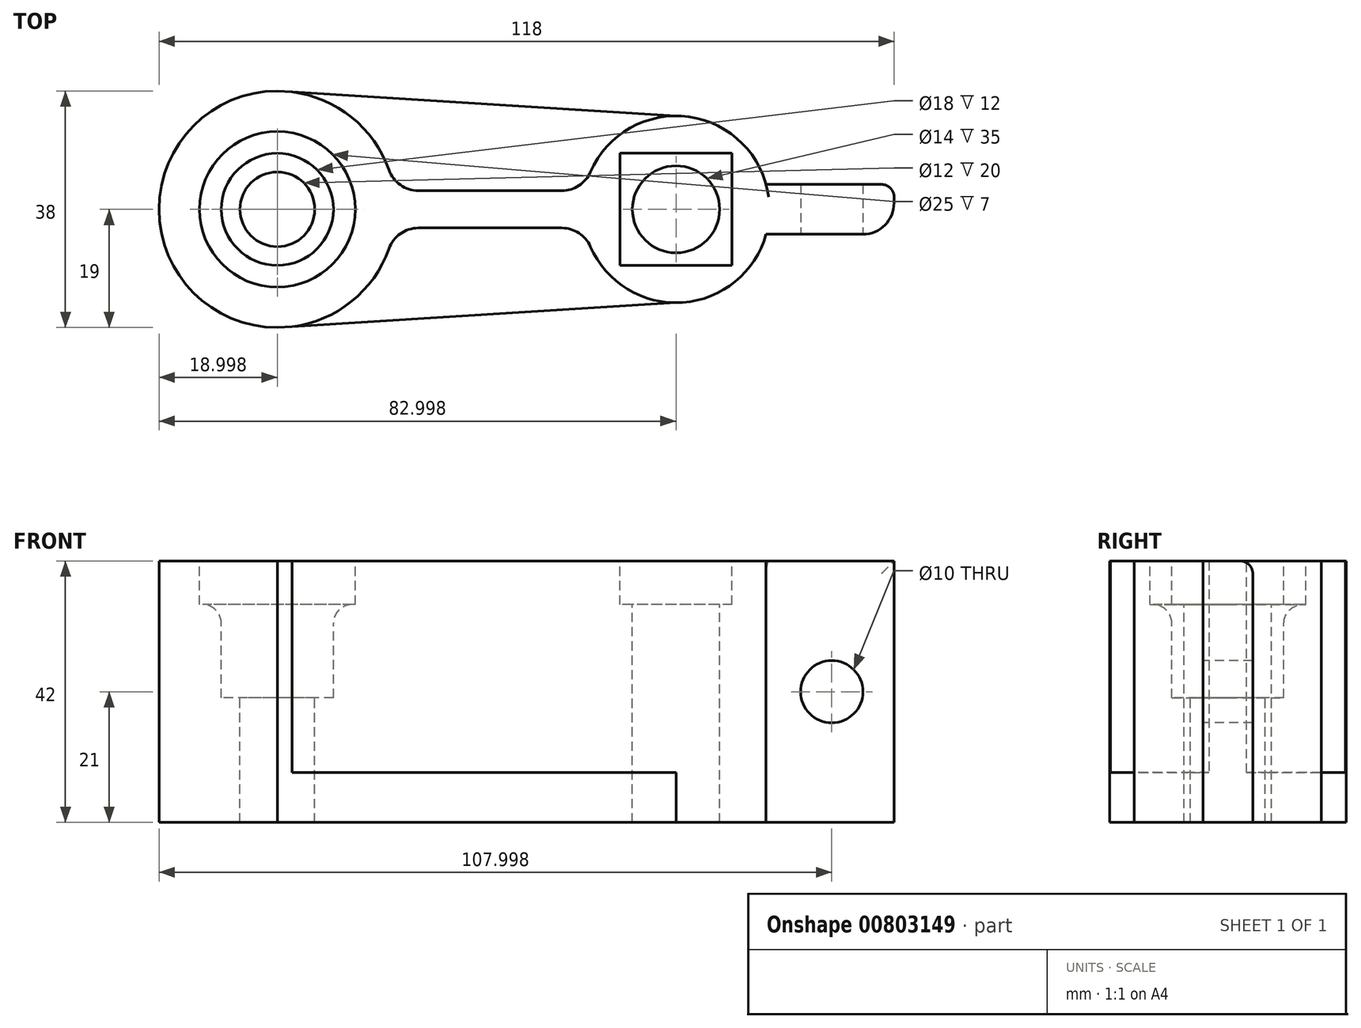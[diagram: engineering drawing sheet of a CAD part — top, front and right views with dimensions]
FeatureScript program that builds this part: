
annotation { "Feature Type Name" : "Feature", "Feature Type Description" : "" }
export const myFeature = defineFeature(function(context is Context, id is Id, definition is map)
    precondition{}
    {
        {
            var Q0;
            Q0=qCreatedBy(makeId("Top.planeOp"),FACE);
            var sketch = newSketch(context, id + "F0", { "sketchPlane" : qUnion([Q0])});
            skArc(sketch, "E0", {"start": v(-57.56, 18.85) * mm, "mid": v(-78.92, 0) * mm, "end": v(-57.56, -18.85) * mm});
            skArc(sketch, "E1", {"start": v(4.08, -15) * mm, "mid": v(19.08, 0) * mm, "end": v(4.08, 15) * mm});
            skLineSegment(sketch, "E2", {"start": v(-59.92, 19) * mm, "end": v(4.08, 15) * mm});
            skLineSegment(sketch, "E3", {"start": v(-59.92, -19) * mm, "end": v(4.08, -15) * mm});
            skLineSegment(sketch, "E4.bottom", {"start": v(39.08, 4) * mm, "end": v(18.53, 4) * mm});
            skLineSegment(sketch, "E4.top", {"start": v(39.08, -4) * mm, "end": v(18.53, -4) * mm});
            skLineSegment(sketch, "E4.left", {"start": v(39.08, 4) * mm, "end": v(39.08, -4) * mm});
            skPoint(sketch, "E4.middle", {"position": v(22.27, 0) * mm});
            skPoint(sketch, "E4.right.start.orphan", {"position": v(5.46, 4) * mm});
            skPoint(sketch, "E5.orphan", {"position": v(5.46, -4) * mm});
            skSolve(sketch);
        }
        {
            var Q0;
            {var subQ0=sQuery(id+"F0.wireOp",EDGE,"E2");var subQ7=sQuery(id+"F0.wireOp",EDGE,"E0");var subQ8=makeQuery(id+"F0.imprint","INTERSECT",VERTEX,{"disambiguationData":[OD(1.0)],"derivedFrom":[subQ7,subQ0]});Q0=makeQuery(id+"F0.imprint","IMPRINT",FACE,{"disambiguationData":[TD([[makeQuery(id+"F0.imprint","IMPRINT",EDGE,{"disambiguationData":[TD([[subQ8,-1.0]])],"derivedFrom":subQ7}),1.0]])]});}
            var Q1;
            {var subQ0=sQuery(id+"F0.wireOp",EDGE,"E4.bottom");Q1=makeQuery(id+"F0.imprint","IMPRINT",FACE,{"disambiguationData":[TD([[makeQuery(id+"F0.imprint","IMPRINT",EDGE,{"derivedFrom":subQ0}),1.0]])]});}
            extrude(context, id + "F1", {"entities" : qUnion([Q0, Q1]), "depth" : 21 * mm, "offsetDistance" : 25 * mm, "hasSecondDirection" : true, "secondDirectionOppositeDirection" : true, "secondDirectionDepth" : 21 * mm});
        }
        {
            var Q0;
            Q0=makeQuery(id+"F1.opExtrude","CAP_FACE",FACE,{"disambiguationData":[OSD([sQuery(id+"F0.wireOp",EDGE,"E0"),sQuery(id+"F0.wireOp",EDGE,"E1"),sQuery(id+"F0.wireOp",EDGE,"E2"),sQuery(id+"F0.wireOp",EDGE,"E3"),sQuery(id+"F0.wireOp",EDGE,"E4.bottom"),sQuery(id+"F0.wireOp",EDGE,"E4.top"),sQuery(id+"F0.wireOp",EDGE,"E4.left")])],"isStart":false});
            var sketch = newSketch(context, id + "F2", { "sketchPlane" : qUnion([Q0])});
            skArc(sketch, "E6", {"start": v(-59.92, -19) * mm, "mid": v(-47.6, -14.46) * mm, "end": v(-41.16, -3) * mm});
            skArc(sketch, "E7", {"start": v(4.08, 15) * mm, "mid": v(-5.4, 11.62) * mm, "end": v(-10.62, 3) * mm});
            skLineSegment(sketch, "E8.bottom", {"start": v(-41.16, 3) * mm, "end": v(-10.62, 3) * mm});
            skLineSegment(sketch, "E8.top", {"start": v(-41.16, -3) * mm, "end": v(-10.62, -3) * mm});
            skPoint(sketch, "E8.middle", {"position": v(-27.05, 0) * mm});
            skPoint(sketch, "E9.orphan", {"position": v(-47.63, 3) * mm});
            skPoint(sketch, "E10.orphan", {"position": v(-47.63, -3) * mm});
            skPoint(sketch, "E11.orphan", {"position": v(-6.46, 3) * mm});
            skPoint(sketch, "E12.orphan", {"position": v(-6.46, -3) * mm});
            skLineSegment(sketch, "E13", {"start": v(-59.92, 19) * mm, "end": v(4.08, 15) * mm});
            skLineSegment(sketch, "E14", {"start": v(-59.92, -19) * mm, "end": v(4.08, -15) * mm});
            skArc(sketch, "E15.trimOffspring", {"start": v(-41.16, 3) * mm, "mid": v(-47.6, 14.46) * mm, "end": v(-59.92, 19) * mm});
            skArc(sketch, "E16.trimOffspring", {"start": v(-10.62, -3) * mm, "mid": v(-5.4, -11.62) * mm, "end": v(4.08, -15) * mm});
            skSolve(sketch);
        }
        {
            var Q0;
            Q0 = qSketchRegion(id + "F2", true);
            extrude(context, id + "F3", {"entities" : qUnion([Q0]), "operationType" : NewBodyOperationType.REMOVE, "oppositeDirection" : true, "depth" : 34 * mm, "offsetDistance" : 25 * mm});
        }
        {
            var Q0;
            Q0=makeQuery(id+"F1.opExtrude","CAP_FACE",FACE,{"disambiguationData":[OSD([sQuery(id+"F0.wireOp",EDGE,"E0"),sQuery(id+"F0.wireOp",EDGE,"E1"),sQuery(id+"F0.wireOp",EDGE,"E2"),sQuery(id+"F0.wireOp",EDGE,"E3"),sQuery(id+"F0.wireOp",EDGE,"E4.bottom"),sQuery(id+"F0.wireOp",EDGE,"E4.top"),sQuery(id+"F0.wireOp",EDGE,"E4.left")])],"isStart":false});
            var sketch = newSketch(context, id + "F4", { "sketchPlane" : qUnion([Q0])});
            skCircle(sketch, "E17", {"center": v(-59.92, 0) * mm, "radius": 6 * mm});
            skCircle(sketch, "E18", {"center": v(4.08, 0) * mm, "radius": 7 * mm});
            skSolve(sketch);
        }
        {
            var Q0;
            Q0 = qSketchRegion(id + "F4", true);
            extrude(context, id + "F5", {"entities" : qUnion([Q0]), "operationType" : NewBodyOperationType.REMOVE, "oppositeDirection" : true, "depth" : 42 * mm, "offsetDistance" : 25 * mm});
        }
        {
            var Q0;
            Q0=makeQuery(id+"F1.opExtrude","CAP_FACE",FACE,{"disambiguationData":[OSD([sQuery(id+"F0.wireOp",EDGE,"E0"),sQuery(id+"F0.wireOp",EDGE,"E1"),sQuery(id+"F0.wireOp",EDGE,"E2"),sQuery(id+"F0.wireOp",EDGE,"E3"),sQuery(id+"F0.wireOp",EDGE,"E4.bottom"),sQuery(id+"F0.wireOp",EDGE,"E4.top"),sQuery(id+"F0.wireOp",EDGE,"E4.left")])],"isStart":false});
            var sketch = newSketch(context, id + "F6", { "sketchPlane" : qUnion([Q0])});
            skCircle(sketch, "E19", {"center": v(-59.92, 0) * mm, "radius": 9 * mm});
            skSolve(sketch);
        }
        {
            var Q0;
            Q0=makeQuery(id+"F6.imprint","IMPRINT",FACE,{"disambiguationData":[TD([[makeQuery(id+"F6.imprint","IMPRINT",EDGE,{"derivedFrom":sQuery(id+"F6.wireOp",EDGE,"E19")}),1.0]])]});
            extrude(context, id + "F7", {"entities" : qUnion([Q0]), "operationType" : NewBodyOperationType.REMOVE, "oppositeDirection" : true, "depth" : 22 * mm, "offsetDistance" : 25 * mm});
        }
        {
            var Q0;
            Q0=makeQuery(id+"F1.opExtrude","CAP_FACE",FACE,{"disambiguationData":[OSD([sQuery(id+"F0.wireOp",EDGE,"E0"),sQuery(id+"F0.wireOp",EDGE,"E1"),sQuery(id+"F0.wireOp",EDGE,"E2"),sQuery(id+"F0.wireOp",EDGE,"E3"),sQuery(id+"F0.wireOp",EDGE,"E4.bottom"),sQuery(id+"F0.wireOp",EDGE,"E4.top"),sQuery(id+"F0.wireOp",EDGE,"E4.left")])],"isStart":false});
            var sketch = newSketch(context, id + "F8", { "sketchPlane" : qUnion([Q0])});
            skLineSegment(sketch, "E20.bottom", {"start": v(13.08, 9) * mm, "end": v(-4.92, 9) * mm});
            skLineSegment(sketch, "E20.top", {"start": v(13.08, -9) * mm, "end": v(-4.92, -9) * mm});
            skLineSegment(sketch, "E20.left", {"start": v(13.08, 9) * mm, "end": v(13.08, -9) * mm});
            skLineSegment(sketch, "E20.right", {"start": v(-4.92, 9) * mm, "end": v(-4.92, -9) * mm});
            skPoint(sketch, "E20.middle", {"position": v(4.08, 0) * mm});
            skSolve(sketch);
        }
        {
            var Q0;
            Q0=makeQuery(id+"F8.imprint","IMPRINT",FACE,{"disambiguationData":[TD([[makeQuery(id+"F8.imprint","IMPRINT",EDGE,{"derivedFrom":sQuery(id+"F8.wireOp",EDGE,"E20.bottom")}),1.0]])]});
            extrude(context, id + "F9", {"entities" : qUnion([Q0]), "operationType" : NewBodyOperationType.REMOVE, "oppositeDirection" : true, "depth" : 7 * mm, "offsetDistance" : 25 * mm});
        }
        {
            var Q0;
            Q0=makeQuery(id+"F1.opExtrude","CAP_FACE",FACE,{"disambiguationData":[OSD([sQuery(id+"F0.wireOp",EDGE,"E0"),sQuery(id+"F0.wireOp",EDGE,"E1"),sQuery(id+"F0.wireOp",EDGE,"E2"),sQuery(id+"F0.wireOp",EDGE,"E3"),sQuery(id+"F0.wireOp",EDGE,"E4.bottom"),sQuery(id+"F0.wireOp",EDGE,"E4.top"),sQuery(id+"F0.wireOp",EDGE,"E4.left")])],"isStart":false});
            var sketch = newSketch(context, id + "F10", { "sketchPlane" : qUnion([Q0])});
            skCircle(sketch, "E21", {"center": v(-59.92, 0) * mm, "radius": 12.5 * mm});
            skSolve(sketch);
        }
        {
            var Q0;
            Q0 = qSketchRegion(id + "F10", true);
            extrude(context, id + "F11", {"entities" : qUnion([Q0]), "operationType" : NewBodyOperationType.REMOVE, "oppositeDirection" : true, "depth" : 7 * mm, "offsetDistance" : 25 * mm});
        }
        {
            var Q0;
            Q0=makeQuery(id+"F1.opExtrude","SWEPT_FACE",FACE,{"disambiguationData":[OSD([sQuery(id+"F0.wireOp",EDGE,"E4.top")])]});
            var sketch = newSketch(context, id + "F12", { "sketchPlane" : qUnion([Q0])});
            skCircle(sketch, "E22", {"center": v(29.08, 0) * mm, "radius": 5 * mm});
            skSolve(sketch);
        }
        {
            var Q0;
            Q0 = qSketchRegion(id + "F12", true);
            extrude(context, id + "F13", {"entities" : qUnion([Q0]), "operationType" : NewBodyOperationType.REMOVE, "oppositeDirection" : true, "depth" : 8 * mm, "offsetDistance" : 25 * mm, "hasSecondDirection" : true, "secondDirectionOppositeDirection" : false, "secondDirectionDepth" : 8 * mm});
        }
        {
            var Q0;
            Q0=makeQuery(id+"F3.boolean.opBoolean","COPY",EDGE,{"derivedFrom":makeQuery(id+"F3.opExtrude","SWEPT_EDGE",EDGE,{"disambiguationData":[OSD([sQuery(id+"F2.wireOp",EDGE,"E6"),sQuery(id+"F2.wireOp",EDGE,"E8.top")])]})});
            var Q1;
            Q1=makeQuery(id+"F3.boolean.opBoolean","COPY",EDGE,{"derivedFrom":makeQuery(id+"F3.opExtrude","SWEPT_EDGE",EDGE,{"disambiguationData":[OSD([sQuery(id+"F2.wireOp",EDGE,"E8.top"),sQuery(id+"F2.wireOp",EDGE,"E16.trimOffspring")])]})});
            var Q2;
            Q2=makeQuery(id+"F3.boolean.opBoolean","COPY",EDGE,{"derivedFrom":makeQuery(id+"F3.opExtrude","SWEPT_EDGE",EDGE,{"disambiguationData":[OSD([sQuery(id+"F2.wireOp",EDGE,"E7"),sQuery(id+"F2.wireOp",EDGE,"E8.bottom")])]})});
            var Q3;
            Q3=makeQuery(id+"F3.boolean.opBoolean","COPY",EDGE,{"derivedFrom":makeQuery(id+"F3.opExtrude","SWEPT_EDGE",EDGE,{"disambiguationData":[OSD([sQuery(id+"F2.wireOp",EDGE,"E8.bottom"),sQuery(id+"F2.wireOp",EDGE,"E15.trimOffspring")])]})});
            var Q4;
            Q4=makeQuery(id+"F11.boolean.opBoolean","COPY",EDGE,{"derivedFrom":makeQuery(id+"F11.opExtrude","CAP_EDGE",EDGE,{"disambiguationData":[OSD([sQuery(id+"F10.wireOp",EDGE,"E21")])],"isStart":true})});
            var Q5;
            Q5=makeQuery(id+"F1.opExtrude","SWEPT_EDGE",EDGE,{"disambiguationData":[OSD([sQuery(id+"F0.wireOp",EDGE,"E4.top"),sQuery(id+"F0.wireOp",EDGE,"E4.left")])]});
            fillet(context, id + "F14", {"entities" : qUnion([Q0, Q1, Q2, Q3, Q4, Q5]), "radius" : 5 * mm, "tangentPropagation" : true, "allowEdgeOverflow" : false});
        }
        {
            var Q0;
            Q0=makeQuery(id+"F9.boolean.opBoolean","COPY",EDGE,{"derivedFrom":makeQuery(id+"F9.opExtrude","CAP_EDGE",EDGE,{"disambiguationData":[OSD([sQuery(id+"F8.wireOp",EDGE,"E20.right")])],"isStart":true})});
            var Q1;
            Q1=makeQuery(id+"F9.boolean.opBoolean","COPY",EDGE,{"derivedFrom":makeQuery(id+"F9.opExtrude","CAP_EDGE",EDGE,{"disambiguationData":[OSD([sQuery(id+"F8.wireOp",EDGE,"E20.bottom")])],"isStart":true})});
            var Q2;
            Q2=makeQuery(id+"F9.boolean.opBoolean","COPY",EDGE,{"derivedFrom":makeQuery(id+"F9.opExtrude","CAP_EDGE",EDGE,{"disambiguationData":[OSD([sQuery(id+"F8.wireOp",EDGE,"E20.left")])],"isStart":true})});
            var Q3;
            Q3=makeQuery(id+"F9.boolean.opBoolean","COPY",EDGE,{"derivedFrom":makeQuery(id+"F9.opExtrude","CAP_EDGE",EDGE,{"disambiguationData":[OSD([sQuery(id+"F8.wireOp",EDGE,"E20.top")])],"isStart":true})});
            var Q4;
            Q4=makeQuery(id+"F1.opExtrude","CAP_EDGE",EDGE,{"disambiguationData":[OSD([sQuery(id+"F0.wireOp",EDGE,"E4.bottom")])],"isStart":false});
            var Q5;
            Q5=makeQuery(id+"F1.opExtrude","SWEPT_EDGE",EDGE,{"disambiguationData":[OSD([sQuery(id+"F0.wireOp",EDGE,"E4.bottom"),sQuery(id+"F0.wireOp",EDGE,"E4.left")])]});
            fillet(context, id + "F15", {"entities" : qUnion([Q0, Q1, Q2, Q3, Q4, Q5]), "radius" : 2 * mm, "tangentPropagation" : true, "allowEdgeOverflow" : false});
        }
        {
            var Q0;
            Q0=makeQuery(id+"F11.boolean.opBoolean","INTERSECT",EDGE,{"derivedFrom":[makeQuery(id+"F7.boolean.opBoolean","COPY",FACE,{"derivedFrom":makeQuery(id+"F7.opExtrude","SWEPT_FACE",FACE,{"disambiguationData":[OSD([sQuery(id+"F6.wireOp",EDGE,"E19")])]})}),makeQuery(id+"F11.opExtrude","CAP_FACE",FACE,{"disambiguationData":[OSD([sQuery(id+"F10.wireOp",EDGE,"E21")])],"isStart":false})]});
            var Q1;
            Q1=makeQuery(id+"F7.boolean.opBoolean","COPY",EDGE,{"derivedFrom":makeQuery(id+"F7.opExtrude","CAP_EDGE",EDGE,{"disambiguationData":[OSD([sQuery(id+"F4.wireOp",EDGE,"E17")])],"isStart":false})});
            fillet(context, id + "F16", {"entities" : qUnion([Q0, Q1]), "radius" : 3 * mm, "tangentPropagation" : true, "allowEdgeOverflow" : false});
        }
    });
